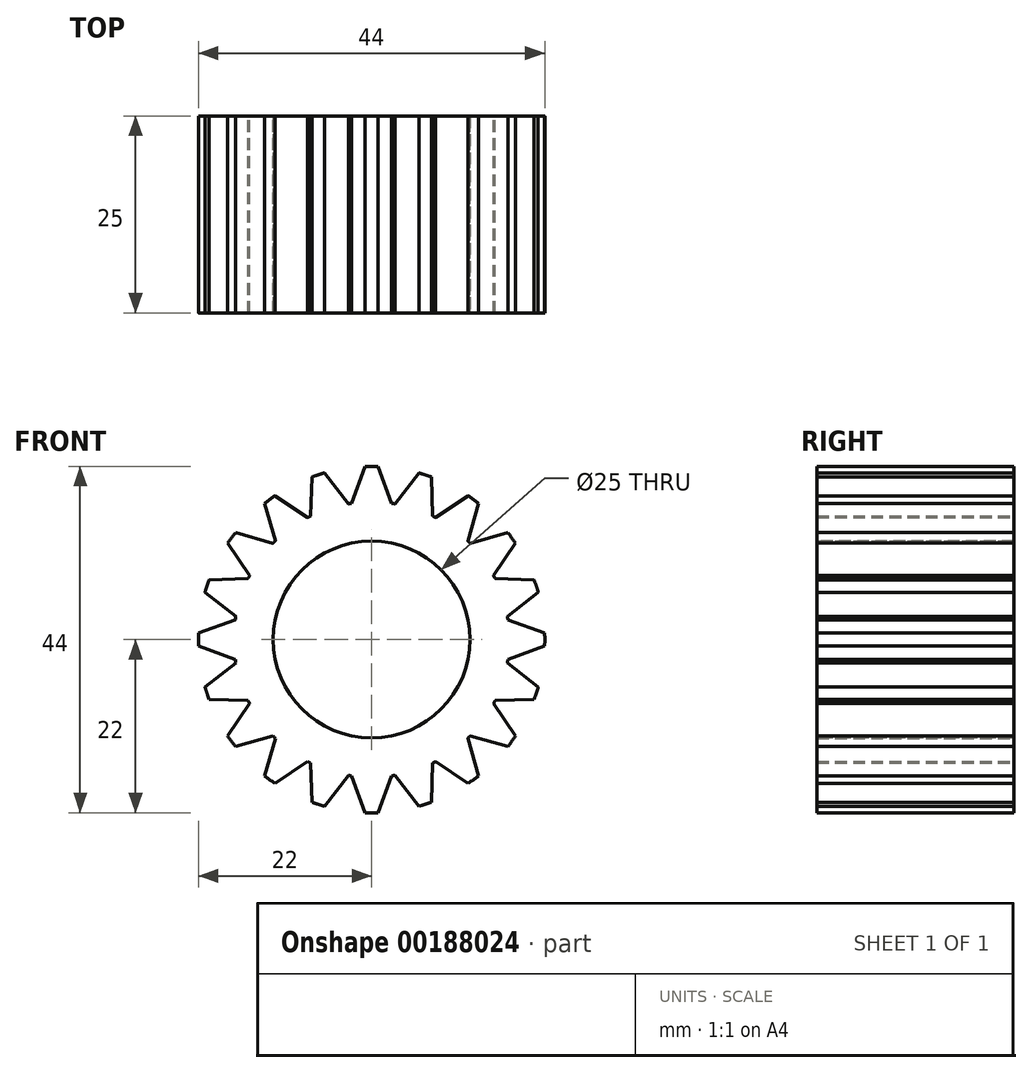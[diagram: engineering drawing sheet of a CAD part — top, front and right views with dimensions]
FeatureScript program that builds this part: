
annotation { "Feature Type Name" : "Feature", "Feature Type Description" : "" }
export const myFeature = defineFeature(function(context is Context, id is Id, definition is map)
    precondition{}
    {
        {
            var Q0;
            Q0=qCreatedBy(makeId("Front.planeOp"),FACE);
            var sketch = newSketch(context, id + "F0", { "sketchPlane" : qUnion([Q0])});
            skCircle(sketch, "E0", {"center": v(0, 0) * mm, "radius": 17.5 * mm});
            skArc(sketch, "E1", {"start": v(0.83, 21.98) * mm, "mid": v(0, 22) * mm, "end": v(-0.83, 21.98) * mm});
            skCircle(sketch, "E2", {"center": v(0, 0) * mm, "radius": 20 * mm, "construction": true});
            skLineSegment(sketch, "E3", {"start": v(0, 9.97) * mm, "end": v(0, 25.2) * mm, "construction": true});
            skLineSegment(sketch, "E4", {"start": v(-2.52, 17.32) * mm, "end": v(-0.83, 21.98) * mm});
            skLineSegment(sketch, "E5.MirrorCS", {"start": v(1.57, 19.94) * mm, "end": v(0.83, 21.98) * mm});
            skPoint(sketch, "E6.orphan", {"position": v(-1.57, 19.94) * mm});
            skPoint(sketch, "E7.orphan", {"position": v(2.52, 17.32) * mm});
            skLineSegment(sketch, "E8", {"start": v(1.57, 19.94) * mm, "end": v(2.52, 17.32) * mm});
            skSolve(sketch);
        }
        {
            var Q0;
            Q0 = qSketchRegion(id + "F0", true);
            extrude(context, id + "F1", {"entities" : qUnion([Q0]), "depth" : 25 * mm});
        }
        {
            var Q0;
            Q0=qCreatedBy(makeId("Right.planeOp"),FACE);
            var sketch = newSketch(context, id + "F2", { "sketchPlane" : qUnion([Q0])});
            skLineSegment(sketch, "E9", {"start": v(-60.1, 0) * mm, "end": v(-42.78, 0) * mm, "construction": true});
            skSolve(sketch);
        }
        {
            var Q0;
            Q0=makeQuery(id+"F1.opExtrude","SWEPT_BODY",BODY,{"disambiguationData":[OSD([sQuery(id+"F0.wireOp",EDGE,"E0"),sQuery(id+"F0.wireOp",EDGE,"E1"),sQuery(id+"F0.wireOp",EDGE,"E4"),sQuery(id+"F0.wireOp",EDGE,"E5.MirrorCS"),sQuery(id+"F0.wireOp",EDGE,"E8")])]});
            var Q1;
            Q1=sQuery(id+"F2.wireOp",EDGE,"E9");
            circularPattern(context, id + "F3", {"entities" : qUnion([Q0]), "axis" : qUnion([Q1]), "angle" : 18 * degree, "instanceCount" : 20});
        }
        {
            var Q0;
            Q0=makeQuery(id+"F1.opExtrude","SWEPT_BODY",BODY,{"disambiguationData":[OSD([sQuery(id+"F0.wireOp",EDGE,"E0"),sQuery(id+"F0.wireOp",EDGE,"E1"),sQuery(id+"F0.wireOp",EDGE,"E4"),sQuery(id+"F0.wireOp",EDGE,"E5.MirrorCS"),sQuery(id+"F0.wireOp",EDGE,"E8")])]});
            var Q1;
            Q1=makeQuery(id+"F3.opPattern","COPY",BODY,{"derivedFrom":makeQuery(id+"F1.opExtrude","SWEPT_BODY",BODY,{"disambiguationData":[OSD([sQuery(id+"F0.wireOp",EDGE,"E0"),sQuery(id+"F0.wireOp",EDGE,"E1"),sQuery(id+"F0.wireOp",EDGE,"E4"),sQuery(id+"F0.wireOp",EDGE,"E5.MirrorCS"),sQuery(id+"F0.wireOp",EDGE,"E8")])]}),"instanceName":"19"});
            var Q2;
            Q2=makeQuery(id+"F3.opPattern","COPY",BODY,{"derivedFrom":makeQuery(id+"F1.opExtrude","SWEPT_BODY",BODY,{"disambiguationData":[OSD([sQuery(id+"F0.wireOp",EDGE,"E0"),sQuery(id+"F0.wireOp",EDGE,"E1"),sQuery(id+"F0.wireOp",EDGE,"E4"),sQuery(id+"F0.wireOp",EDGE,"E5.MirrorCS"),sQuery(id+"F0.wireOp",EDGE,"E8")])]}),"instanceName":"3"});
            var Q3;
            Q3=makeQuery(id+"F3.opPattern","COPY",BODY,{"derivedFrom":makeQuery(id+"F1.opExtrude","SWEPT_BODY",BODY,{"disambiguationData":[OSD([sQuery(id+"F0.wireOp",EDGE,"E0"),sQuery(id+"F0.wireOp",EDGE,"E1"),sQuery(id+"F0.wireOp",EDGE,"E4"),sQuery(id+"F0.wireOp",EDGE,"E5.MirrorCS"),sQuery(id+"F0.wireOp",EDGE,"E8")])]}),"instanceName":"11"});
            var Q4;
            Q4=makeQuery(id+"F3.opPattern","COPY",BODY,{"derivedFrom":makeQuery(id+"F1.opExtrude","SWEPT_BODY",BODY,{"disambiguationData":[OSD([sQuery(id+"F0.wireOp",EDGE,"E0"),sQuery(id+"F0.wireOp",EDGE,"E1"),sQuery(id+"F0.wireOp",EDGE,"E4"),sQuery(id+"F0.wireOp",EDGE,"E5.MirrorCS"),sQuery(id+"F0.wireOp",EDGE,"E8")])]}),"instanceName":"14"});
            var Q5;
            Q5=makeQuery(id+"F3.opPattern","COPY",BODY,{"derivedFrom":makeQuery(id+"F1.opExtrude","SWEPT_BODY",BODY,{"disambiguationData":[OSD([sQuery(id+"F0.wireOp",EDGE,"E0"),sQuery(id+"F0.wireOp",EDGE,"E1"),sQuery(id+"F0.wireOp",EDGE,"E4"),sQuery(id+"F0.wireOp",EDGE,"E5.MirrorCS"),sQuery(id+"F0.wireOp",EDGE,"E8")])]}),"instanceName":"5"});
            var Q6;
            Q6=makeQuery(id+"F3.opPattern","COPY",BODY,{"derivedFrom":makeQuery(id+"F1.opExtrude","SWEPT_BODY",BODY,{"disambiguationData":[OSD([sQuery(id+"F0.wireOp",EDGE,"E0"),sQuery(id+"F0.wireOp",EDGE,"E1"),sQuery(id+"F0.wireOp",EDGE,"E4"),sQuery(id+"F0.wireOp",EDGE,"E5.MirrorCS"),sQuery(id+"F0.wireOp",EDGE,"E8")])]}),"instanceName":"4"});
            var Q7;
            Q7=makeQuery(id+"F3.opPattern","COPY",BODY,{"derivedFrom":makeQuery(id+"F1.opExtrude","SWEPT_BODY",BODY,{"disambiguationData":[OSD([sQuery(id+"F0.wireOp",EDGE,"E0"),sQuery(id+"F0.wireOp",EDGE,"E1"),sQuery(id+"F0.wireOp",EDGE,"E4"),sQuery(id+"F0.wireOp",EDGE,"E5.MirrorCS"),sQuery(id+"F0.wireOp",EDGE,"E8")])]}),"instanceName":"8"});
            var Q8;
            Q8=makeQuery(id+"F3.opPattern","COPY",BODY,{"derivedFrom":makeQuery(id+"F1.opExtrude","SWEPT_BODY",BODY,{"disambiguationData":[OSD([sQuery(id+"F0.wireOp",EDGE,"E0"),sQuery(id+"F0.wireOp",EDGE,"E1"),sQuery(id+"F0.wireOp",EDGE,"E4"),sQuery(id+"F0.wireOp",EDGE,"E5.MirrorCS"),sQuery(id+"F0.wireOp",EDGE,"E8")])]}),"instanceName":"6"});
            var Q9;
            Q9=makeQuery(id+"F3.opPattern","COPY",BODY,{"derivedFrom":makeQuery(id+"F1.opExtrude","SWEPT_BODY",BODY,{"disambiguationData":[OSD([sQuery(id+"F0.wireOp",EDGE,"E0"),sQuery(id+"F0.wireOp",EDGE,"E1"),sQuery(id+"F0.wireOp",EDGE,"E4"),sQuery(id+"F0.wireOp",EDGE,"E5.MirrorCS"),sQuery(id+"F0.wireOp",EDGE,"E8")])]}),"instanceName":"7"});
            var Q10;
            Q10=makeQuery(id+"F3.opPattern","COPY",BODY,{"derivedFrom":makeQuery(id+"F1.opExtrude","SWEPT_BODY",BODY,{"disambiguationData":[OSD([sQuery(id+"F0.wireOp",EDGE,"E0"),sQuery(id+"F0.wireOp",EDGE,"E1"),sQuery(id+"F0.wireOp",EDGE,"E4"),sQuery(id+"F0.wireOp",EDGE,"E5.MirrorCS"),sQuery(id+"F0.wireOp",EDGE,"E8")])]}),"instanceName":"9"});
            var Q11;
            Q11=makeQuery(id+"F3.opPattern","COPY",BODY,{"derivedFrom":makeQuery(id+"F1.opExtrude","SWEPT_BODY",BODY,{"disambiguationData":[OSD([sQuery(id+"F0.wireOp",EDGE,"E0"),sQuery(id+"F0.wireOp",EDGE,"E1"),sQuery(id+"F0.wireOp",EDGE,"E4"),sQuery(id+"F0.wireOp",EDGE,"E5.MirrorCS"),sQuery(id+"F0.wireOp",EDGE,"E8")])]}),"instanceName":"10"});
            var Q12;
            Q12=makeQuery(id+"F3.opPattern","COPY",BODY,{"derivedFrom":makeQuery(id+"F1.opExtrude","SWEPT_BODY",BODY,{"disambiguationData":[OSD([sQuery(id+"F0.wireOp",EDGE,"E0"),sQuery(id+"F0.wireOp",EDGE,"E1"),sQuery(id+"F0.wireOp",EDGE,"E4"),sQuery(id+"F0.wireOp",EDGE,"E5.MirrorCS"),sQuery(id+"F0.wireOp",EDGE,"E8")])]}),"instanceName":"12"});
            var Q13;
            Q13=makeQuery(id+"F3.opPattern","COPY",BODY,{"derivedFrom":makeQuery(id+"F1.opExtrude","SWEPT_BODY",BODY,{"disambiguationData":[OSD([sQuery(id+"F0.wireOp",EDGE,"E0"),sQuery(id+"F0.wireOp",EDGE,"E1"),sQuery(id+"F0.wireOp",EDGE,"E4"),sQuery(id+"F0.wireOp",EDGE,"E5.MirrorCS"),sQuery(id+"F0.wireOp",EDGE,"E8")])]}),"instanceName":"15"});
            var Q14;
            Q14=makeQuery(id+"F3.opPattern","COPY",BODY,{"derivedFrom":makeQuery(id+"F1.opExtrude","SWEPT_BODY",BODY,{"disambiguationData":[OSD([sQuery(id+"F0.wireOp",EDGE,"E0"),sQuery(id+"F0.wireOp",EDGE,"E1"),sQuery(id+"F0.wireOp",EDGE,"E4"),sQuery(id+"F0.wireOp",EDGE,"E5.MirrorCS"),sQuery(id+"F0.wireOp",EDGE,"E8")])]}),"instanceName":"18"});
            var Q15;
            Q15=makeQuery(id+"F3.opPattern","COPY",BODY,{"derivedFrom":makeQuery(id+"F1.opExtrude","SWEPT_BODY",BODY,{"disambiguationData":[OSD([sQuery(id+"F0.wireOp",EDGE,"E0"),sQuery(id+"F0.wireOp",EDGE,"E1"),sQuery(id+"F0.wireOp",EDGE,"E4"),sQuery(id+"F0.wireOp",EDGE,"E5.MirrorCS"),sQuery(id+"F0.wireOp",EDGE,"E8")])]}),"instanceName":"13"});
            var Q16;
            Q16=makeQuery(id+"F3.opPattern","COPY",BODY,{"derivedFrom":makeQuery(id+"F1.opExtrude","SWEPT_BODY",BODY,{"disambiguationData":[OSD([sQuery(id+"F0.wireOp",EDGE,"E0"),sQuery(id+"F0.wireOp",EDGE,"E1"),sQuery(id+"F0.wireOp",EDGE,"E4"),sQuery(id+"F0.wireOp",EDGE,"E5.MirrorCS"),sQuery(id+"F0.wireOp",EDGE,"E8")])]}),"instanceName":"2"});
            var Q17;
            Q17=makeQuery(id+"F3.opPattern","COPY",BODY,{"derivedFrom":makeQuery(id+"F1.opExtrude","SWEPT_BODY",BODY,{"disambiguationData":[OSD([sQuery(id+"F0.wireOp",EDGE,"E0"),sQuery(id+"F0.wireOp",EDGE,"E1"),sQuery(id+"F0.wireOp",EDGE,"E4"),sQuery(id+"F0.wireOp",EDGE,"E5.MirrorCS"),sQuery(id+"F0.wireOp",EDGE,"E8")])]}),"instanceName":"16"});
            var Q18;
            Q18=makeQuery(id+"F3.opPattern","COPY",BODY,{"derivedFrom":makeQuery(id+"F1.opExtrude","SWEPT_BODY",BODY,{"disambiguationData":[OSD([sQuery(id+"F0.wireOp",EDGE,"E0"),sQuery(id+"F0.wireOp",EDGE,"E1"),sQuery(id+"F0.wireOp",EDGE,"E4"),sQuery(id+"F0.wireOp",EDGE,"E5.MirrorCS"),sQuery(id+"F0.wireOp",EDGE,"E8")])]}),"instanceName":"17"});
            var Q19;
            Q19=makeQuery(id+"F3.opPattern","COPY",BODY,{"derivedFrom":makeQuery(id+"F1.opExtrude","SWEPT_BODY",BODY,{"disambiguationData":[OSD([sQuery(id+"F0.wireOp",EDGE,"E0"),sQuery(id+"F0.wireOp",EDGE,"E1"),sQuery(id+"F0.wireOp",EDGE,"E4"),sQuery(id+"F0.wireOp",EDGE,"E5.MirrorCS"),sQuery(id+"F0.wireOp",EDGE,"E8")])]}),"instanceName":"1"});
            booleanBodies(context, id + "F4", {"operationType" : BooleanOperationType.UNION, "tools" : qUnion([Q0, Q1, Q2, Q3, Q4, Q5, Q6, Q7, Q8, Q9, Q10, Q11, Q12, Q13, Q14, Q15, Q16, Q17, Q18, Q19])});
        }
        {
            var Q0;
            {var subQ0=makeQuery(id+"F1.opExtrude","CAP_FACE",FACE,{"disambiguationData":[OSD([sQuery(id+"F0.wireOp",EDGE,"E0"),sQuery(id+"F0.wireOp",EDGE,"E1"),sQuery(id+"F0.wireOp",EDGE,"E4"),sQuery(id+"F0.wireOp",EDGE,"E5.MirrorCS"),sQuery(id+"F0.wireOp",EDGE,"E8")])],"isStart":false});Q0=makeQuery(id+"F4.opBoolean","MERGE",FACE,{"derivedFrom":[subQ0,makeQuery(id+"F3.opPattern","COPY",FACE,{"derivedFrom":subQ0,"instanceName":"1"}),makeQuery(id+"F3.opPattern","COPY",FACE,{"derivedFrom":subQ0,"instanceName":"2"}),makeQuery(id+"F3.opPattern","COPY",FACE,{"derivedFrom":subQ0,"instanceName":"3"}),makeQuery(id+"F3.opPattern","COPY",FACE,{"derivedFrom":subQ0,"instanceName":"4"}),makeQuery(id+"F3.opPattern","COPY",FACE,{"derivedFrom":subQ0,"instanceName":"5"}),makeQuery(id+"F3.opPattern","COPY",FACE,{"derivedFrom":subQ0,"instanceName":"6"}),makeQuery(id+"F3.opPattern","COPY",FACE,{"derivedFrom":subQ0,"instanceName":"7"}),makeQuery(id+"F3.opPattern","COPY",FACE,{"derivedFrom":subQ0,"instanceName":"8"}),makeQuery(id+"F3.opPattern","COPY",FACE,{"derivedFrom":subQ0,"instanceName":"9"}),makeQuery(id+"F3.opPattern","COPY",FACE,{"derivedFrom":subQ0,"instanceName":"10"}),makeQuery(id+"F3.opPattern","COPY",FACE,{"derivedFrom":subQ0,"instanceName":"11"}),makeQuery(id+"F3.opPattern","COPY",FACE,{"derivedFrom":subQ0,"instanceName":"12"}),makeQuery(id+"F3.opPattern","COPY",FACE,{"derivedFrom":subQ0,"instanceName":"13"}),makeQuery(id+"F3.opPattern","COPY",FACE,{"derivedFrom":subQ0,"instanceName":"14"}),makeQuery(id+"F3.opPattern","COPY",FACE,{"derivedFrom":subQ0,"instanceName":"15"}),makeQuery(id+"F3.opPattern","COPY",FACE,{"derivedFrom":subQ0,"instanceName":"16"}),makeQuery(id+"F3.opPattern","COPY",FACE,{"derivedFrom":subQ0,"instanceName":"17"}),makeQuery(id+"F3.opPattern","COPY",FACE,{"derivedFrom":subQ0,"instanceName":"18"}),makeQuery(id+"F3.opPattern","COPY",FACE,{"derivedFrom":subQ0,"instanceName":"19"})]});}
            var sketch = newSketch(context, id + "F5", { "sketchPlane" : qUnion([Q0])});
            skCircle(sketch, "E10", {"center": v(0, 0) * mm, "radius": 12.5 * mm});
            skSolve(sketch);
        }
        {
            var Q0;
            Q0 = qSketchRegion(id + "F5", true);
            extrude(context, id + "F6", {"entities" : qUnion([Q0]), "operationType" : NewBodyOperationType.REMOVE, "oppositeDirection" : true, "depth" : 53.5 * mm});
        }
    });
